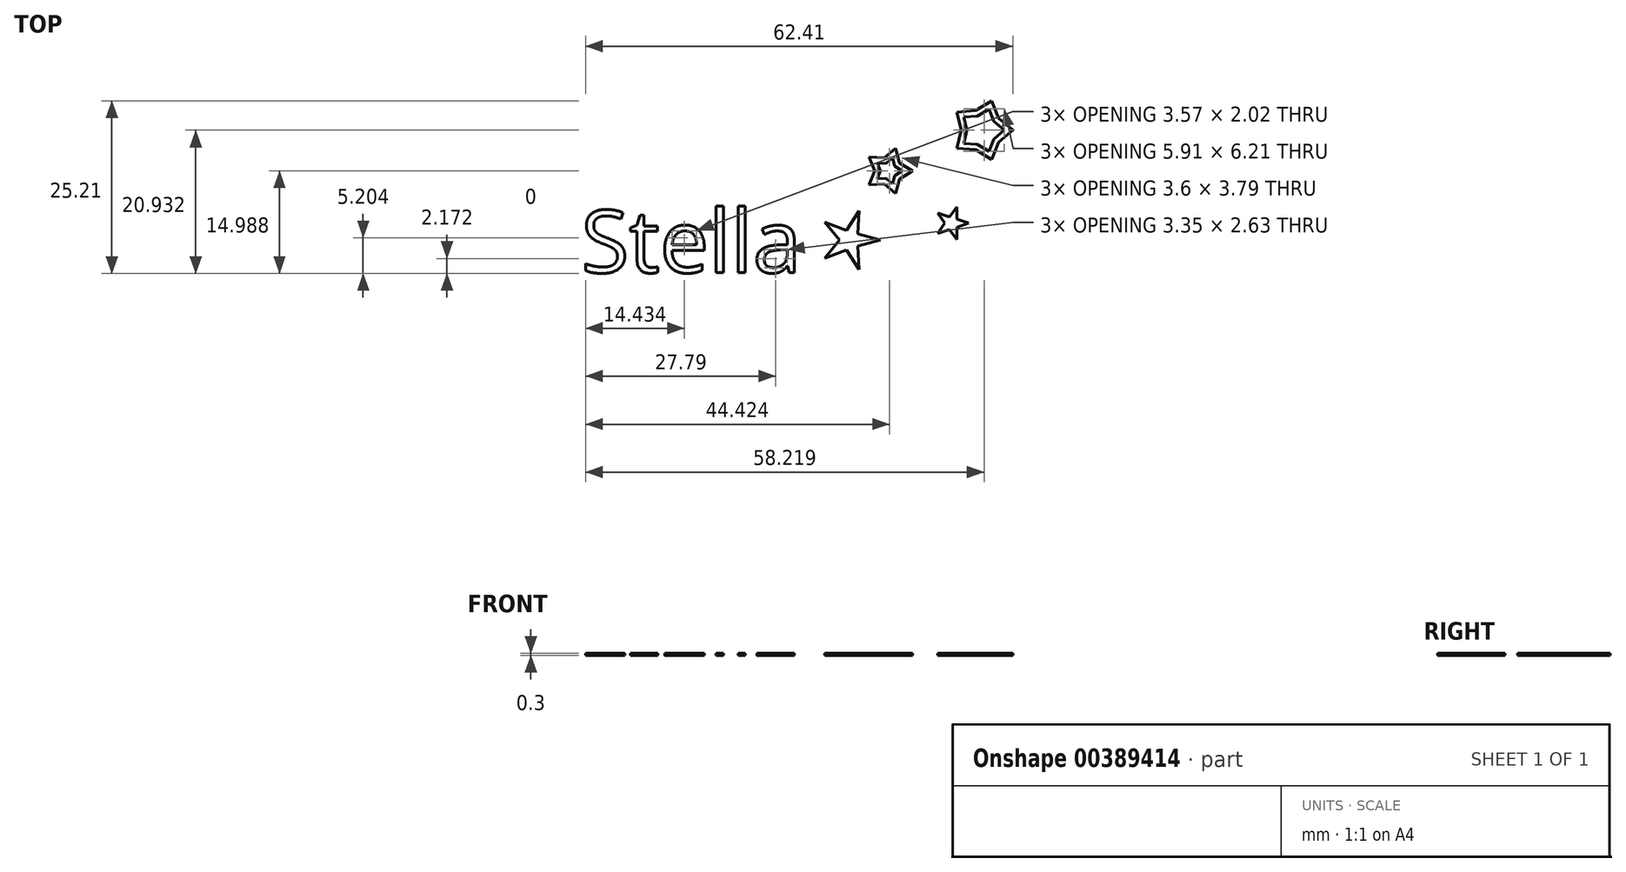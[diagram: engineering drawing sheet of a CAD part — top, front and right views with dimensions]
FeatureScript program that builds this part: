
annotation { "Feature Type Name" : "Feature", "Feature Type Description" : "" }
export const myFeature = defineFeature(function(context is Context, id is Id, definition is map)
    precondition{}
    {
        {
            var Q0;
            Q0=qCreatedBy(makeId("Top.planeOp"),FACE);
            var sketch = newSketch(context, id + "F0", { "sketchPlane" : qUnion([Q0])});
            skCircle(sketch, "E0.cCircle", {"center": v(46.45, 16.36) * mm, "radius": 4.5 * mm, "construction": true});
            skLineSegment(sketch, "E0.0", {"start": v(50.95, 16.36) * mm, "end": v(47.84, 12.08) * mm, "construction": true});
            skLineSegment(sketch, "E0.1", {"start": v(47.84, 12.08) * mm, "end": v(42.8, 13.72) * mm, "construction": true});
            skLineSegment(sketch, "E0.2", {"start": v(42.8, 13.72) * mm, "end": v(42.8, 19) * mm, "construction": true});
            skLineSegment(sketch, "E0.3", {"start": v(42.8, 19) * mm, "end": v(47.84, 20.64) * mm, "construction": true});
            skLineSegment(sketch, "E0.4", {"start": v(47.84, 20.64) * mm, "end": v(50.95, 16.36) * mm, "construction": true});
            skCircle(sketch, "E1.cCircle", {"center": v(46.45, 16.36) * mm, "radius": 3 * mm, "construction": true});
            skLineSegment(sketch, "E1.0", {"start": v(48.87, 18.13) * mm, "end": v(48.87, 14.6) * mm, "construction": true});
            skLineSegment(sketch, "E1.1", {"start": v(48.87, 14.6) * mm, "end": v(45.52, 13.5) * mm, "construction": true});
            skLineSegment(sketch, "E1.2", {"start": v(45.52, 13.5) * mm, "end": v(43.45, 16.36) * mm, "construction": true});
            skLineSegment(sketch, "E1.3", {"start": v(43.45, 16.36) * mm, "end": v(45.52, 19.21) * mm, "construction": true});
            skLineSegment(sketch, "E1.4", {"start": v(45.52, 19.21) * mm, "end": v(48.87, 18.13) * mm, "construction": true});
            skLineSegment(sketch, "E2", {"start": v(42.8, 19) * mm, "end": v(43.45, 16.36) * mm});
            skLineSegment(sketch, "E3", {"start": v(42.8, 13.72) * mm, "end": v(43.45, 16.36) * mm});
            skLineSegment(sketch, "E4", {"start": v(42.8, 13.72) * mm, "end": v(45.52, 13.5) * mm});
            skLineSegment(sketch, "E5", {"start": v(45.52, 13.5) * mm, "end": v(47.84, 12.08) * mm});
            skLineSegment(sketch, "E6", {"start": v(47.84, 12.08) * mm, "end": v(48.87, 14.6) * mm});
            skLineSegment(sketch, "E7", {"start": v(48.87, 14.6) * mm, "end": v(50.95, 16.36) * mm});
            skLineSegment(sketch, "E8", {"start": v(50.95, 16.36) * mm, "end": v(48.87, 18.13) * mm});
            skLineSegment(sketch, "E9", {"start": v(48.87, 18.13) * mm, "end": v(47.84, 20.64) * mm});
            skLineSegment(sketch, "E10", {"start": v(47.84, 20.64) * mm, "end": v(45.52, 19.21) * mm});
            skLineSegment(sketch, "E11", {"start": v(45.52, 19.21) * mm, "end": v(42.8, 19) * mm});
            skCircle(sketch, "E12.cCircle", {"center": v(32.77, 10.42) * mm, "radius": 3.5 * mm, "construction": true});
            skLineSegment(sketch, "E12.0", {"start": v(36.27, 10.42) * mm, "end": v(33.86, 7.09) * mm, "construction": true});
            skLineSegment(sketch, "E12.1", {"start": v(33.86, 7.09) * mm, "end": v(29.94, 8.36) * mm, "construction": true});
            skLineSegment(sketch, "E12.2", {"start": v(29.94, 8.36) * mm, "end": v(29.94, 12.47) * mm, "construction": true});
            skLineSegment(sketch, "E12.3", {"start": v(29.94, 12.47) * mm, "end": v(33.86, 13.75) * mm, "construction": true});
            skLineSegment(sketch, "E12.4", {"start": v(33.86, 13.75) * mm, "end": v(36.27, 10.42) * mm, "construction": true});
            skCircle(sketch, "E13.cCircle", {"center": v(32.77, 10.42) * mm, "radius": 2 * mm, "construction": true});
            skLineSegment(sketch, "E13.0", {"start": v(34.4, 11.6) * mm, "end": v(34.4, 9.24) * mm, "construction": true});
            skLineSegment(sketch, "E13.1", {"start": v(34.4, 9.24) * mm, "end": v(32.16, 8.52) * mm, "construction": true});
            skLineSegment(sketch, "E13.2", {"start": v(32.16, 8.52) * mm, "end": v(30.77, 10.42) * mm, "construction": true});
            skLineSegment(sketch, "E13.3", {"start": v(30.77, 10.42) * mm, "end": v(32.16, 12.32) * mm, "construction": true});
            skLineSegment(sketch, "E13.4", {"start": v(32.16, 12.32) * mm, "end": v(34.4, 11.6) * mm, "construction": true});
            skLineSegment(sketch, "E14", {"start": v(29.94, 12.47) * mm, "end": v(30.77, 10.42) * mm});
            skLineSegment(sketch, "E15", {"start": v(29.94, 8.36) * mm, "end": v(30.77, 10.42) * mm});
            skLineSegment(sketch, "E16", {"start": v(29.94, 8.36) * mm, "end": v(32.16, 8.52) * mm});
            skLineSegment(sketch, "E17", {"start": v(32.16, 8.52) * mm, "end": v(33.86, 7.09) * mm});
            skLineSegment(sketch, "E18", {"start": v(33.86, 7.09) * mm, "end": v(34.4, 9.24) * mm});
            skLineSegment(sketch, "E19", {"start": v(34.4, 9.24) * mm, "end": v(36.27, 10.42) * mm});
            skLineSegment(sketch, "E20", {"start": v(36.27, 10.42) * mm, "end": v(34.4, 11.6) * mm});
            skLineSegment(sketch, "E21", {"start": v(34.4, 11.6) * mm, "end": v(33.86, 13.75) * mm});
            skLineSegment(sketch, "E22", {"start": v(33.86, 13.75) * mm, "end": v(32.16, 12.32) * mm});
            skLineSegment(sketch, "E23", {"start": v(32.16, 12.32) * mm, "end": v(29.94, 12.47) * mm});
            skCircle(sketch, "E24.cCircle", {"center": v(41.99, 2.77) * mm, "radius": 2.5 * mm, "construction": true});
            skLineSegment(sketch, "E24.0", {"start": v(44.49, 2.77) * mm, "end": v(42.76, 0.39) * mm, "construction": true});
            skLineSegment(sketch, "E24.1", {"start": v(42.76, 0.39) * mm, "end": v(39.97, 1.3) * mm, "construction": true});
            skLineSegment(sketch, "E24.2", {"start": v(39.97, 1.3) * mm, "end": v(39.97, 4.24) * mm, "construction": true});
            skLineSegment(sketch, "E24.3", {"start": v(39.97, 4.24) * mm, "end": v(42.76, 5.14) * mm, "construction": true});
            skLineSegment(sketch, "E24.4", {"start": v(42.76, 5.14) * mm, "end": v(44.49, 2.77) * mm, "construction": true});
            skCircle(sketch, "E25.cCircle", {"center": v(41.99, 2.77) * mm, "radius": 1 * mm, "construction": true});
            skLineSegment(sketch, "E25.0", {"start": v(42.8, 3.36) * mm, "end": v(42.8, 2.18) * mm, "construction": true});
            skLineSegment(sketch, "E25.1", {"start": v(42.8, 2.18) * mm, "end": v(41.68, 1.82) * mm, "construction": true});
            skLineSegment(sketch, "E25.2", {"start": v(41.68, 1.82) * mm, "end": v(40.99, 2.77) * mm, "construction": true});
            skLineSegment(sketch, "E25.3", {"start": v(40.99, 2.77) * mm, "end": v(41.68, 3.72) * mm, "construction": true});
            skLineSegment(sketch, "E25.4", {"start": v(41.68, 3.72) * mm, "end": v(42.8, 3.36) * mm, "construction": true});
            skLineSegment(sketch, "E26", {"start": v(39.97, 4.24) * mm, "end": v(40.99, 2.77) * mm});
            skLineSegment(sketch, "E27", {"start": v(39.97, 1.3) * mm, "end": v(40.99, 2.77) * mm});
            skLineSegment(sketch, "E28", {"start": v(39.97, 1.3) * mm, "end": v(41.68, 1.82) * mm});
            skLineSegment(sketch, "E29", {"start": v(41.68, 1.82) * mm, "end": v(42.76, 0.39) * mm});
            skLineSegment(sketch, "E30", {"start": v(42.76, 0.39) * mm, "end": v(42.8, 2.18) * mm});
            skLineSegment(sketch, "E31", {"start": v(42.8, 2.18) * mm, "end": v(44.49, 2.77) * mm});
            skLineSegment(sketch, "E32", {"start": v(44.49, 2.77) * mm, "end": v(42.8, 3.36) * mm});
            skLineSegment(sketch, "E33", {"start": v(42.8, 3.36) * mm, "end": v(42.76, 5.14) * mm});
            skLineSegment(sketch, "E34", {"start": v(42.76, 5.14) * mm, "end": v(41.68, 3.72) * mm});
            skLineSegment(sketch, "E35", {"start": v(41.68, 3.72) * mm, "end": v(39.97, 4.24) * mm});
            skCircle(sketch, "E36.cCircle", {"center": v(27.11, 0.31) * mm, "radius": 4.5 * mm, "construction": true});
            skLineSegment(sketch, "E36.0", {"start": v(31.61, 0.31) * mm, "end": v(28.5, -3.97) * mm, "construction": true});
            skLineSegment(sketch, "E36.1", {"start": v(28.5, -3.97) * mm, "end": v(23.47, -2.33) * mm, "construction": true});
            skLineSegment(sketch, "E36.2", {"start": v(23.47, -2.33) * mm, "end": v(23.47, 2.96) * mm, "construction": true});
            skLineSegment(sketch, "E36.3", {"start": v(23.47, 2.96) * mm, "end": v(28.5, 4.6) * mm, "construction": true});
            skLineSegment(sketch, "E36.4", {"start": v(28.5, 4.6) * mm, "end": v(31.61, 0.31) * mm, "construction": true});
            skCircle(sketch, "E37.cCircle", {"center": v(27.11, 0.31) * mm, "radius": 1.5 * mm, "construction": true});
            skLineSegment(sketch, "E37.0", {"start": v(28.32, 1.2) * mm, "end": v(28.32, -0.57) * mm, "construction": true});
            skLineSegment(sketch, "E37.1", {"start": v(28.32, -0.57) * mm, "end": v(26.65, -1.11) * mm, "construction": true});
            skLineSegment(sketch, "E37.2", {"start": v(26.65, -1.11) * mm, "end": v(25.61, 0.31) * mm, "construction": true});
            skLineSegment(sketch, "E37.3", {"start": v(25.61, 0.31) * mm, "end": v(26.65, 1.74) * mm, "construction": true});
            skLineSegment(sketch, "E37.4", {"start": v(26.65, 1.74) * mm, "end": v(28.32, 1.2) * mm, "construction": true});
            skLineSegment(sketch, "E38", {"start": v(23.47, 2.96) * mm, "end": v(25.61, 0.31) * mm});
            skLineSegment(sketch, "E39", {"start": v(23.47, -2.33) * mm, "end": v(25.61, 0.31) * mm});
            skLineSegment(sketch, "E40", {"start": v(23.47, -2.33) * mm, "end": v(26.65, -1.11) * mm});
            skLineSegment(sketch, "E41", {"start": v(26.65, -1.11) * mm, "end": v(28.5, -3.97) * mm});
            skLineSegment(sketch, "E42", {"start": v(28.5, -3.97) * mm, "end": v(28.32, -0.57) * mm});
            skLineSegment(sketch, "E43", {"start": v(28.32, -0.57) * mm, "end": v(31.61, 0.31) * mm});
            skLineSegment(sketch, "E44", {"start": v(31.61, 0.31) * mm, "end": v(28.32, 1.2) * mm});
            skLineSegment(sketch, "E45", {"start": v(28.32, 1.2) * mm, "end": v(28.5, 4.6) * mm});
            skLineSegment(sketch, "E46", {"start": v(28.5, 4.6) * mm, "end": v(26.65, 1.74) * mm});
            skLineSegment(sketch, "E47", {"start": v(26.65, 1.74) * mm, "end": v(23.47, 2.96) * mm});
            skLineSegment(sketch, "E48.0", {"start": v(48.2, 17.64) * mm, "end": v(47.46, 19.47) * mm});
            skLineSegment(sketch, "E48.1", {"start": v(49.71, 16.36) * mm, "end": v(48.2, 17.64) * mm});
            skLineSegment(sketch, "E48.2", {"start": v(47.46, 19.47) * mm, "end": v(45.77, 18.43) * mm});
            skLineSegment(sketch, "E48.3", {"start": v(48.2, 15.08) * mm, "end": v(49.71, 16.36) * mm});
            skLineSegment(sketch, "E48.4", {"start": v(47.46, 13.26) * mm, "end": v(48.2, 15.08) * mm});
            skLineSegment(sketch, "E48.5", {"start": v(45.77, 14.3) * mm, "end": v(47.46, 13.26) * mm});
            skLineSegment(sketch, "E48.6", {"start": v(45.77, 18.43) * mm, "end": v(43.8, 18.28) * mm});
            skLineSegment(sketch, "E48.7", {"start": v(43.8, 18.28) * mm, "end": v(44.27, 16.36) * mm});
            skLineSegment(sketch, "E48.8", {"start": v(43.8, 14.44) * mm, "end": v(44.27, 16.36) * mm});
            skLineSegment(sketch, "E48.9", {"start": v(43.8, 14.44) * mm, "end": v(45.77, 14.3) * mm});
            skLineSegment(sketch, "E49.0", {"start": v(33.7, 11.09) * mm, "end": v(33.39, 12.31) * mm});
            skLineSegment(sketch, "E49.1", {"start": v(34.76, 10.42) * mm, "end": v(33.7, 11.09) * mm});
            skLineSegment(sketch, "E49.2", {"start": v(33.39, 12.31) * mm, "end": v(32.42, 11.5) * mm});
            skLineSegment(sketch, "E49.3", {"start": v(33.7, 9.75) * mm, "end": v(34.76, 10.42) * mm});
            skLineSegment(sketch, "E49.4", {"start": v(33.39, 8.53) * mm, "end": v(33.7, 9.75) * mm});
            skLineSegment(sketch, "E49.5", {"start": v(32.42, 9.34) * mm, "end": v(33.39, 8.53) * mm});
            skLineSegment(sketch, "E49.6", {"start": v(32.42, 11.5) * mm, "end": v(31.16, 11.59) * mm});
            skLineSegment(sketch, "E49.7", {"start": v(31.16, 11.59) * mm, "end": v(31.64, 10.42) * mm});
            skLineSegment(sketch, "E49.8", {"start": v(31.16, 9.25) * mm, "end": v(31.64, 10.42) * mm});
            skLineSegment(sketch, "E49.9", {"start": v(31.16, 9.25) * mm, "end": v(32.42, 9.34) * mm});
            skText(sketch, "E50", { "text": "Stella", "fontName": "OpenSans-Regular.ttf"});
            const initialGuessF0  = {"E50": [-0.01212, -0.00444, 1, 0, 0.00918]};
            skSetInitialGuess(sketch, initialGuessF0);
            skSolve(sketch);
        }
        {
            var Q0;
            Q0=qSketchRegion(id+"F0",true);
            extrude(context, id + "F1", {"entities" : qUnion([Q0]), "depth" : 0.3 * mm});
        }
    });
